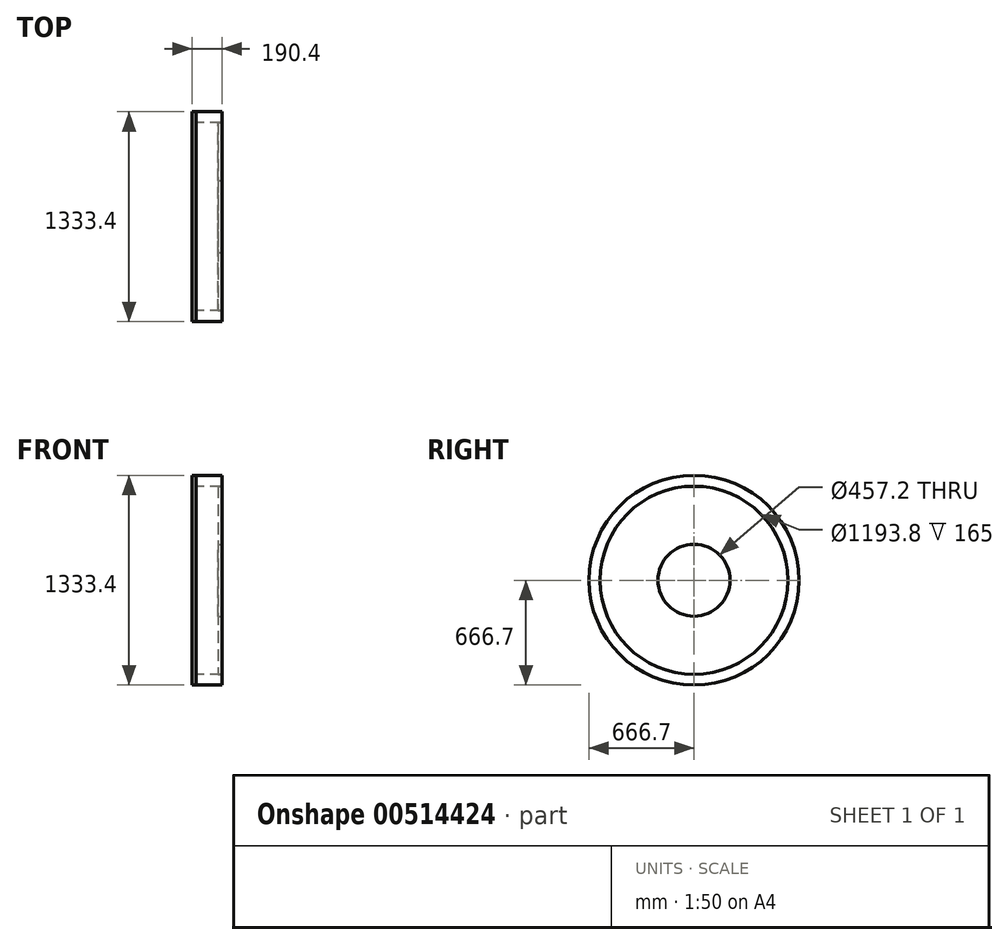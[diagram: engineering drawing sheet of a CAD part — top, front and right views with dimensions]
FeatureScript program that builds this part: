
annotation { "Feature Type Name" : "Feature", "Feature Type Description" : "" }
export const myFeature = defineFeature(function(context is Context, id is Id, definition is map)
    precondition{}
    {
        {
            var Q0;
            Q0=qCreatedBy(makeId("Front.planeOp"),FACE);
            var sketch = newSketch(context, id + "F0", { "sketchPlane" : qUnion([Q0])});
            skCircle(sketch, "E0", {"center": v(0, 0) * mm, "radius": 50.8 * mm, "construction": true});
            skCircle(sketch, "E1.0", {"center": v(0, 0) * mm, "radius": 69.8 * mm, "construction": true});
            skLineSegment(sketch, "E2", {"start": v(69.8, 0) * mm, "end": v(95.2, 0) * mm, "construction": true});
            skLineSegment(sketch, "E3.bottom", {"start": v(95.2, 0) * mm, "end": v(-69.8, 0) * mm});
            skLineSegment(sketch, "E3.top", {"start": v(95.2, 69.8) * mm, "end": v(-69.8, 69.8) * mm});
            skLineSegment(sketch, "E3.left", {"start": v(95.2, 69.8) * mm, "end": v(95.2, 0) * mm});
            skLineSegment(sketch, "E3.right", {"start": v(-69.8, 69.8) * mm, "end": v(-69.8, 0) * mm});
            skLineSegment(sketch, "E4.bottom", {"start": v(-69.8, 0) * mm, "end": v(95.2, 0) * mm, "construction": true});
            skLineSegment(sketch, "E4.top", {"start": v(-69.8, -1193.8) * mm, "end": v(95.2, -1193.8) * mm, "construction": true});
            skLineSegment(sketch, "E4.left", {"start": v(-69.8, 0) * mm, "end": v(-69.8, -1193.8) * mm, "construction": true});
            skLineSegment(sketch, "E4.right", {"start": v(95.2, 0) * mm, "end": v(95.2, -1193.8) * mm, "construction": true});
            skLineSegment(sketch, "E5", {"start": v(-69.8, -596.9) * mm, "end": v(95.2, -596.9) * mm, "construction": true});
            skLineSegment(sketch, "E6.bottom", {"start": v(-69.8, 69.8) * mm, "end": v(-95.2, 69.8) * mm});
            skLineSegment(sketch, "E6.top", {"start": v(-69.8, 0) * mm, "end": v(-95.2, 0) * mm});
            skLineSegment(sketch, "E6.right", {"start": v(-95.2, 69.8) * mm, "end": v(-95.2, 0) * mm});
            skPoint(sketch, "E7", {"position": v(0, -596.9) * mm});
            skLineSegment(sketch, "E8.bottom", {"start": v(-95.2, 0) * mm, "end": v(-120.6, 0) * mm});
            skLineSegment(sketch, "E8.top", {"start": v(-95.2, 69.8) * mm, "end": v(-120.6, 69.8) * mm});
            skLineSegment(sketch, "E8.left", {"start": v(-95.2, 0) * mm, "end": v(-95.2, 69.8) * mm});
            skLineSegment(sketch, "E8.right", {"start": v(-120.6, 0) * mm, "end": v(-120.6, 69.8) * mm});
            skSolve(sketch);
        }
        {
            var Q0;
            Q0=makeQuery(id+"F0.imprint","IMPRINT",FACE,{"disambiguationData":[TD([[makeQuery(id+"F0.imprint","IMPRINT",EDGE,{"derivedFrom":sQuery(id+"F0.wireOp",EDGE,"E3.bottom")}),-1.0]])]});
            var Q1;
            Q1=sQuery(id+"F0.wireOp",EDGE,"E5");
            revolve(context, id + "F1", {"entities" : qUnion([Q0]), "axis" : qUnion([Q1]), "revolveType" : RevolveType.FULL});
        }
        {
            var Q0;
            Q0=makeQuery(id+"F1.opRevolve","SWEPT_FACE",FACE,{"disambiguationData":[OSD([sQuery(id+"F0.wireOp",EDGE,"E3.left")])]});
            var sketch = newSketch(context, id + "F2", { "sketchPlane" : qUnion([Q0])});
            skCircle(sketch, "E9", {"center": v(0, -596.9) * mm, "radius": 228.6 * mm});
            skSolve(sketch);
        }
        {
            var Q0;
            Q0=makeQuery(id+"F2.imprint","IMPRINT",FACE,{"disambiguationData":[TD([[makeQuery(id+"F2.imprint","IMPRINT",EDGE,{"derivedFrom":sQuery(id+"F2.wireOp",EDGE,"E9")}),-1.0]])]});
            extrude(context, id + "F3", {"entities" : qUnion([Q0]), "oppositeDirection" : true, "depth" : 25.4 * mm, "offsetDistance" : 25.4 * mm});
        }
        {
            var Q0;
            Q0=makeQuery(id+"F1.opRevolve","SWEPT_FACE",FACE,{"disambiguationData":[OSD([sQuery(id+"F0.wireOp",EDGE,"E3.right")])]});
            var sketch = newSketch(context, id + "F4", { "sketchPlane" : qUnion([Q0])});
            skCircle(sketch, "E10", {"center": v(0, -596.9) * mm, "radius": 666.7 * mm});
            skSolve(sketch);
        }
        {
            var Q0;
            Q0 = qSketchRegion(id + "F4", true);
            extrude(context, id + "F5", {"entities" : qUnion([Q0]), "depth" : 25.4 * mm, "offsetDistance" : 25.4 * mm});
        }
    });
